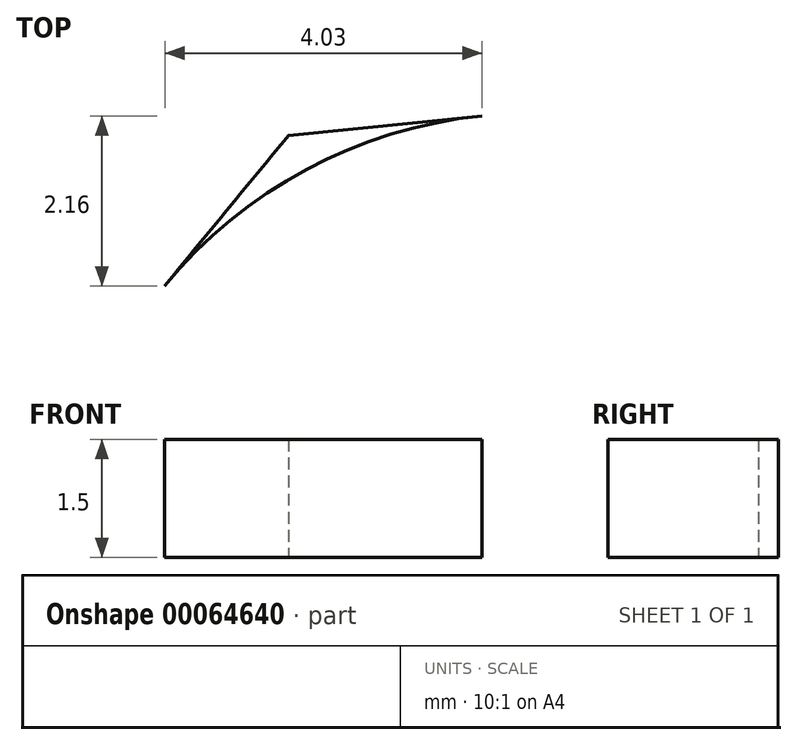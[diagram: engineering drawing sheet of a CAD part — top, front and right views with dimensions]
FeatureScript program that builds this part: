
annotation { "Feature Type Name" : "Feature", "Feature Type Description" : "" }
export const myFeature = defineFeature(function(context is Context, id is Id, definition is map)
    precondition{}
    {
        {
            var Q0;
            Q0=qCreatedBy(makeId("Top.planeOp"),FACE);
            var sketch = newSketch(context, id + "F0", { "sketchPlane" : qUnion([Q0])});
            skLineSegment(sketch, "E0", {"start": v(-116.5, 0) * mm, "end": v(139.03, 0) * mm, "construction": true});
            skLineSegment(sketch, "E1.0", {"start": v(-116.5, -90) * mm, "end": v(139.03, -90) * mm, "construction": true});
            skLineSegment(sketch, "E2.0", {"start": v(-116.5, 90) * mm, "end": v(139.03, 90) * mm, "construction": true});
            skLineSegment(sketch, "E3", {"start": v(0, 90) * mm, "end": v(0, -92.69) * mm, "construction": true});
            skLineSegment(sketch, "E4.0", {"start": v(-100, 90) * mm, "end": v(-100, -92.69) * mm, "construction": true});
            skLineSegment(sketch, "E5.0", {"start": v(-120, 90) * mm, "end": v(-120, -92.69) * mm, "construction": true});
            skLineSegment(sketch, "E6.0", {"start": v(120, 90) * mm, "end": v(120, -92.69) * mm, "construction": true});
            skLineSegment(sketch, "E7.0", {"start": v(100, 90) * mm, "end": v(100, -92.69) * mm, "construction": true});
            skFitSpline(sketch, "E8", {"points": [v(-100, 90) * mm, v(-114.02, 69.47) * mm, v(-120, 43.4) * mm, v(-120, 8.31) * mm, v(-100, -90) * mm, v(0, -80.79) * mm], "startDerivative": vector(-114.58, -138.92) * mm, "endDerivative": vector(433.2, 151.03) * mm});
            skFitSpline(sketch, "E9", {"points": [v(0, 78.79) * mm, v(-34.86, 79.72) * mm, v(-58.45, 90) * mm, v(-100, 90) * mm], "startDerivative": vector(-110.99, -8.68) * mm, "endDerivative": vector(-123.02, -12.63) * mm});
            skArc(sketch, "E10.filletArc", {"start": v(-97.54, 90.25) * mm, "mid": v(-99.77, 89.57) * mm, "end": v(-101.57, 88.09) * mm});
            skFitSpline(sketch, "E11.MirrorCS", {"points": [v(0, 78.79) * mm, v(34.86, 79.72) * mm, v(58.45, 90) * mm, v(100, 90) * mm], "startDerivative": vector(110.99, -8.68) * mm, "endDerivative": vector(123.02, -12.63) * mm});
            skFitSpline(sketch, "E12.MirrorCS", {"points": [v(100, 90) * mm, v(114.02, 69.47) * mm, v(120, 43.4) * mm, v(120, 8.31) * mm, v(100, -90) * mm, v(0, -80.79) * mm], "startDerivative": vector(114.58, -138.92) * mm, "endDerivative": vector(-433.2, 151.03) * mm});
            skArc(sketch, "E13.MirrorCS", {"start": v(97.54, 90.25) * mm, "mid": v(99.77, 89.57) * mm, "end": v(101.57, 88.09) * mm});
            skFitSpline(sketch, "E14.0", {"points": [v(0.16, 76.8) * mm, v(-2.16, 76.61) * mm, v(-6.8, 76.25) * mm, v(-13.69, 75.85) * mm, v(-20.42, 75.74) * mm, v(-25.82, 76.02) * mm, v(-29.97, 76.55) * mm, v(-32.48, 77.03) * mm, v(-34.44, 77.51) * mm, v(-36.35, 78.06) * mm, v(-38.65, 78.88) * mm, v(-41.26, 80) * mm, v(-44.61, 81.61) * mm, v(-47.82, 83.32) * mm, v(-51.02, 84.95) * mm, v(-53.45, 86.09) * mm, v(-55.94, 87.11) * mm, v(-58.1, 87.84) * mm, v(-59.9, 88.32) * mm, v(-61.76, 88.75) * mm, v(-64.2, 89.18) * mm, v(-67.3, 89.53) * mm, v(-71.61, 89.8) * mm, v(-77.33, 89.83) * mm, v(-84.6, 89.45) * mm, v(-92.12, 88.8) * mm, v(-97.23, 88.27) * mm, v(-99.8, 88.01) * mm]});
            skFitSpline(sketch, "E15.0", {"points": [v(-0.16, 76.8) * mm, v(2.16, 76.61) * mm, v(6.8, 76.25) * mm, v(13.69, 75.85) * mm, v(20.42, 75.74) * mm, v(25.82, 76.02) * mm, v(29.97, 76.55) * mm, v(32.48, 77.03) * mm, v(34.44, 77.51) * mm, v(36.35, 78.06) * mm, v(38.65, 78.88) * mm, v(41.26, 80) * mm, v(44.61, 81.61) * mm, v(47.82, 83.32) * mm, v(51.02, 84.95) * mm, v(53.45, 86.09) * mm, v(55.94, 87.11) * mm, v(58.1, 87.84) * mm, v(59.9, 88.32) * mm, v(61.76, 88.75) * mm, v(64.2, 89.18) * mm, v(67.3, 89.53) * mm, v(71.61, 89.8) * mm, v(77.33, 89.83) * mm, v(84.6, 89.45) * mm, v(92.12, 88.8) * mm, v(97.23, 88.27) * mm, v(99.8, 88.01) * mm]});
            skFitSpline(sketch, "E16.0", {"points": [v(98.46, 88.73) * mm, v(99.65, 87.28) * mm, v(102.03, 84.4) * mm, v(105.43, 80.03) * mm, v(108.04, 76.27) * mm, v(109.92, 73.15) * mm, v(111.23, 70.74) * mm, v(112.4, 68.25) * mm, v(113.46, 65.66) * mm, v(114.39, 62.97) * mm, v(115.47, 59.3) * mm, v(116.56, 54.56) * mm, v(117.47, 48.83) * mm, v(118.05, 43.2) * mm, v(118.35, 37.81) * mm, v(118.44, 32.29) * mm, v(118.37, 26.22) * mm, v(118.24, 20.4) * mm, v(118.12, 15.08) * mm, v(118.05, 11.45) * mm, v(118, 8.34) * mm, v(117.95, 5.08) * mm, v(117.9, 0.76) * mm, v(117.8, -4.78) * mm, v(117.63, -12.53) * mm, v(117.26, -22.79) * mm, v(116.37, -35.51) * mm, v(114.87, -48.17) * mm, v(112.6, -60.27) * mm, v(109.38, -71.31) * mm, v(105.8, -79.21) * mm, v(102.33, -84.5) * mm, v(99.92, -87.34) * mm, v(97.83, -89.3) * mm, v(95.62, -91.08) * mm, v(91.46, -93.7) * mm, v(84.64, -96.16) * mm, v(75.12, -97.29) * mm, v(64.45, -96.8) * mm, v(52.83, -94.9) * mm, v(40.45, -91.9) * mm, v(23.2, -86.76) * mm, v(9.68, -82.05) * mm, v(0.66, -78.9) * mm]});
            skFitSpline(sketch, "E17.0", {"points": [v(-98.46, 88.73) * mm, v(-99.65, 87.28) * mm, v(-102.03, 84.4) * mm, v(-105.43, 80.03) * mm, v(-108.04, 76.27) * mm, v(-109.92, 73.15) * mm, v(-111.23, 70.74) * mm, v(-112.4, 68.25) * mm, v(-113.46, 65.66) * mm, v(-114.39, 62.97) * mm, v(-115.47, 59.3) * mm, v(-116.56, 54.56) * mm, v(-117.47, 48.83) * mm, v(-118.05, 43.2) * mm, v(-118.35, 37.81) * mm, v(-118.44, 32.29) * mm, v(-118.37, 26.22) * mm, v(-118.24, 20.4) * mm, v(-118.12, 15.08) * mm, v(-118.05, 11.45) * mm, v(-118, 8.34) * mm, v(-117.95, 5.08) * mm, v(-117.9, 0.76) * mm, v(-117.8, -4.78) * mm, v(-117.63, -12.53) * mm, v(-117.26, -22.79) * mm, v(-116.37, -35.51) * mm, v(-114.87, -48.17) * mm, v(-112.6, -60.27) * mm, v(-109.38, -71.31) * mm, v(-105.8, -79.21) * mm, v(-102.33, -84.5) * mm, v(-99.92, -87.34) * mm, v(-97.83, -89.3) * mm, v(-95.62, -91.08) * mm, v(-91.46, -93.7) * mm, v(-84.64, -96.16) * mm, v(-75.12, -97.29) * mm, v(-64.45, -96.8) * mm, v(-52.83, -94.9) * mm, v(-40.45, -91.9) * mm, v(-23.2, -86.76) * mm, v(-9.68, -82.05) * mm, v(-0.66, -78.9) * mm]});
            skFitSpline(sketch, "E18", {"points": [v(-0.66, -78.9) * mm, v(0, -78.63) * mm, v(0.66, -78.9) * mm], "startDerivative": vector(1.32, 0.81) * mm, "endDerivative": vector(1.32, -0.81) * mm});
            skArc(sketch, "E19.filletArc", {"start": v(100.56, 86.17) * mm, "mid": v(98.75, 87.66) * mm, "end": v(96.52, 88.35) * mm});
            skArc(sketch, "E20.filletArc", {"start": v(-96.52, 88.35) * mm, "mid": v(-98.75, 87.66) * mm, "end": v(-100.56, 86.17) * mm});
            skSolve(sketch);
        }
        {
            var Q0;
            Q0=makeQuery(id+"F0.imprint","IMPRINT",FACE,{"disambiguationData":[TD([[makeQuery(id+"F0.imprint","IMPRINT",EDGE,{"derivedFrom":sQuery(id+"F0.wireOp",EDGE,"E8")}),1.0]])]});
            extrude(context, id + "F1", {"entities" : qUnion([Q0]), "depth" : 1.5 * mm});
        }
    });
